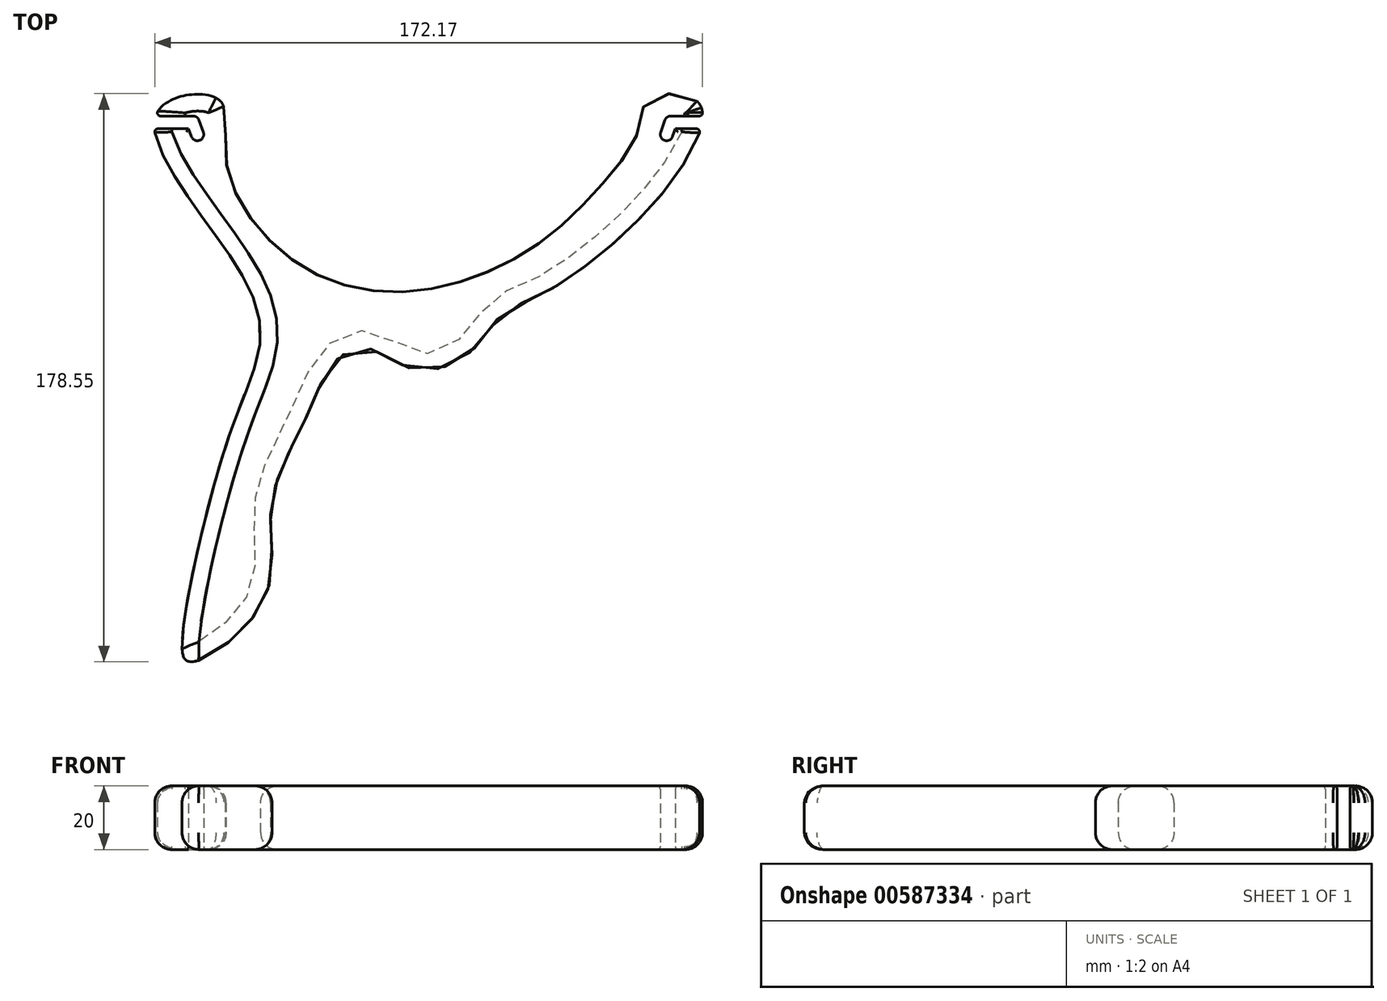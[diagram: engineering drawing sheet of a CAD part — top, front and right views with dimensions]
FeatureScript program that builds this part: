
annotation { "Feature Type Name" : "Feature", "Feature Type Description" : "" }
export const myFeature = defineFeature(function(context is Context, id is Id, definition is map)
    precondition{}
    {
        {
            var Q0;
            Q0=qCreatedBy(makeId("Top.planeOp"),FACE);
            var sketch = newSketch(context, id + "F0", { "sketchPlane" : qUnion([Q0])});
            skFitSpline(sketch, "E0", {"points": [v(-47.93, -12.17) * mm, v(-57.47, -39.46) * mm, v(-72.05, -102.78) * mm, v(-69.37, -109.92) * mm, v(-46.47, -90.68) * mm, v(-44.04, -60.37) * mm, v(-33.84, -34.8) * mm, v(-25.4, -17.36) * mm, v(-14.64, -11.28) * mm, v(2.1, -18.27) * mm, v(21.1, -10.15) * mm, v(28.84, 0) * mm, v(37.64, 3.9) * mm, v(75.58, 33.49) * mm, v(90.24, 65.72) * mm, v(74.78, 66.75) * mm, v(71.07, 56.48) * mm, v(59.13, 39.35) * mm, v(42.22, 23.11) * mm, v(9.4, 7.88) * mm, v(-32.22, 13.06) * mm, v(-58.26, 46.98) * mm, v(-60.8, 66.85) * mm, v(-80.26, 62.1) * mm, v(-53.82, 12.56) * mm, v(-47.93, -12.17) * mm]});
            skLineSegment(sketch, "E1.bottom", {"start": v(-50.8, -23.67) * mm, "end": v(-15.8, -23.67) * mm, "construction": true});
            skLineSegment(sketch, "E1.top", {"start": v(-50.8, -113.67) * mm, "end": v(-15.8, -113.67) * mm, "construction": true});
            skLineSegment(sketch, "E1.left", {"start": v(-50.8, -23.67) * mm, "end": v(-50.8, -113.67) * mm, "construction": true});
            skLineSegment(sketch, "E1.right", {"start": v(-15.8, -23.67) * mm, "end": v(-15.8, -113.67) * mm, "construction": true});
            skLineSegment(sketch, "E2", {"start": v(4, -25.72) * mm, "end": v(34, -25.72) * mm, "construction": true});
            skLineSegment(sketch, "E3", {"start": v(-54.68, 63.24) * mm, "end": v(65.32, 63.24) * mm, "construction": true});
            skLineSegment(sketch, "E4", {"start": v(96.78, 66.75) * mm, "end": v(96.78, 6.75) * mm, "construction": true});
            skSolve(sketch);
        }
        {
            var Q0;
            Q0=makeQuery(id+"F0.imprint","IMPRINT",FACE,{"disambiguationData":[TD([[makeQuery(id+"F0.imprint","IMPRINT",EDGE,{"derivedFrom":sQuery(id+"F0.wireOp",EDGE,"E0")}),1.0]])]});
            var sketch = newSketch(context, id + "F1", { "sketchPlane" : qUnion([Q0])});
            skLineSegment(sketch, "E5", {"start": v(-68.65, 59.57) * mm, "end": v(-67.3, 55.8) * mm});
            skArc(sketch, "E6.0.startCap", {"start": v(-70.53, 58.9) * mm, "mid": v(-69.32, 61.45) * mm, "end": v(-66.77, 60.24) * mm});
            skArc(sketch, "E6.0.endCap", {"start": v(-65.42, 56.48) * mm, "mid": v(-66.63, 53.92) * mm, "end": v(-69.18, 55.13) * mm});
            skLineSegment(sketch, "E6.0.left", {"start": v(-66.77, 60.24) * mm, "end": v(-65.42, 56.48) * mm});
            skLineSegment(sketch, "E6.0.right", {"start": v(-70.53, 58.9) * mm, "end": v(-69.18, 55.13) * mm});
            skLineSegment(sketch, "E7.MirrorCS", {"start": v(81.52, 59.57) * mm, "end": v(80.18, 55.8) * mm});
            skArc(sketch, "E8.0.startCap", {"start": v(79.64, 60.24) * mm, "mid": v(82.2, 61.45) * mm, "end": v(83.4, 58.9) * mm});
            skArc(sketch, "E8.0.endCap", {"start": v(82.06, 55.13) * mm, "mid": v(79.5, 53.92) * mm, "end": v(78.3, 56.48) * mm});
            skLineSegment(sketch, "E8.0.left", {"start": v(83.4, 58.9) * mm, "end": v(82.06, 55.13) * mm});
            skLineSegment(sketch, "E8.0.right", {"start": v(79.64, 60.24) * mm, "end": v(78.3, 56.48) * mm});
            skLineSegment(sketch, "E9", {"start": v(-67.3, 55.8) * mm, "end": v(80.18, 55.8) * mm, "construction": true});
            skLineSegment(sketch, "E10", {"start": v(81.52, 59.57) * mm, "end": v(92.32, 59.57) * mm});
            skArc(sketch, "E11.0.startCap", {"start": v(81.52, 57.57) * mm, "mid": v(79.52, 59.57) * mm, "end": v(81.52, 61.57) * mm});
            skArc(sketch, "E11.0.endCap", {"start": v(92.32, 61.57) * mm, "mid": v(94.32, 59.57) * mm, "end": v(92.32, 57.57) * mm});
            skLineSegment(sketch, "E11.0.left", {"start": v(81.52, 61.57) * mm, "end": v(92.32, 61.57) * mm});
            skLineSegment(sketch, "E11.0.right", {"start": v(81.52, 57.57) * mm, "end": v(92.32, 57.57) * mm});
            skLineSegment(sketch, "E12", {"start": v(-68.65, 59.57) * mm, "end": v(-88.7, 59.57) * mm});
            skArc(sketch, "E13.0.startCap", {"start": v(-68.65, 61.57) * mm, "mid": v(-66.65, 59.57) * mm, "end": v(-68.65, 57.57) * mm});
            skArc(sketch, "E13.0.endCap", {"start": v(-88.7, 57.57) * mm, "mid": v(-90.7, 59.57) * mm, "end": v(-88.7, 61.57) * mm});
            skLineSegment(sketch, "E13.0.left", {"start": v(-68.65, 57.57) * mm, "end": v(-88.7, 57.57) * mm});
            skLineSegment(sketch, "E13.0.right", {"start": v(-68.65, 61.57) * mm, "end": v(-88.7, 61.57) * mm});
            skSolve(sketch);
        }
        {
            var Q0;
            Q0=makeQuery(id+"F0.imprint","IMPRINT",FACE,{"disambiguationData":[TD([[makeQuery(id+"F0.imprint","IMPRINT",EDGE,{"derivedFrom":sQuery(id+"F0.wireOp",EDGE,"E0")}),1.0]])]});
            extrude(context, id + "F2", {"entities" : qUnion([Q0]), "depth" : 20 * mm, "offsetDistance" : 25 * mm});
        }
        {
            var Q0;
            Q0=makeQuery(id+"F2.opExtrude","CAP_EDGE",EDGE,{"disambiguationData":[OSD([sQuery(id+"F0.wireOp",EDGE,"E0")])],"isStart":false});
            var Q1;
            Q1=makeQuery(id+"F2.opExtrude","CAP_EDGE",EDGE,{"disambiguationData":[OSD([sQuery(id+"F0.wireOp",EDGE,"E0")])],"isStart":true});
            fillet(context, id + "F3", {"entities" : qUnion([Q0, Q1]), "radius" : 5.3 * mm, "tangentPropagation" : true, "allowEdgeOverflow" : false});
        }
        {
            var Q0;
            Q0 = qSketchRegion(id + "F1", true);
            extrude(context, id + "F4", {"entities" : qUnion([Q0]), "operationType" : NewBodyOperationType.REMOVE, "endBound" : BoundingType.THROUGH_ALL, "depth" : 25 * mm, "offsetDistance" : 25 * mm});
        }
        {
            var Q0;
            Q0=makeQuery(id+"F4.boolean.opBoolean","INTERSECT",EDGE,{"derivedFrom":[makeQuery(id+"F2.opExtrude","CAP_FACE",FACE,{"disambiguationData":[OSD([sQuery(id+"F0.wireOp",EDGE,"E0")])],"isStart":false}),makeQuery(id+"F4.opExtrude","SWEPT_FACE",FACE,{"disambiguationData":[OSD([sQuery(id+"F1.wireOp",EDGE,"E6.0.right")])]})]});
            var Q1;
            {var subQ0=sQuery(id+"F0.wireOp",EDGE,"E0");Q1=makeQuery(id+"F4.boolean.opBoolean","INTERSECT",EDGE,{"derivedFrom":[makeQuery(id+"F3.opFillet","BLEND_FACE",FACE,{"disambiguationData":[OSD([subQ0]),TDD([makeQuery(id+"F2.opExtrude","CAP_EDGE",EDGE,{"disambiguationData":[OSD([subQ0])],"isStart":true})]),OD(6.0)]}),makeQuery(id+"F4.opExtrude","SWEPT_FACE",FACE,{"disambiguationData":[OSD([sQuery(id+"F1.wireOp",EDGE,"E6.0.left")])]})]});}
            var Q2;
            Q2=makeQuery(id+"F4.boolean.opBoolean","COPY",EDGE,{"derivedFrom":makeQuery(id+"F4.opExtrude","CAP_EDGE",EDGE,{"disambiguationData":[OSD([sQuery(id+"F1.wireOp",EDGE,"E8.0.right")])],"isStart":true})});
            var Q3;
            Q3=makeQuery(id+"F4.boolean.opBoolean","INTERSECT",EDGE,{"derivedFrom":[makeQuery(id+"F2.opExtrude","CAP_FACE",FACE,{"disambiguationData":[OSD([sQuery(id+"F0.wireOp",EDGE,"E0")])],"isStart":false}),makeQuery(id+"F4.opExtrude","SWEPT_FACE",FACE,{"disambiguationData":[OSD([sQuery(id+"F1.wireOp",EDGE,"E8.0.left")])]})]});
            var Q4;
            Q4=makeQuery(id+"F4.boolean.opBoolean","INTERSECT",EDGE,{"derivedFrom":[makeQuery(id+"F2.opExtrude","CAP_FACE",FACE,{"disambiguationData":[OSD([sQuery(id+"F0.wireOp",EDGE,"E0")])],"isStart":false}),makeQuery(id+"F4.opExtrude","SWEPT_FACE",FACE,{"disambiguationData":[OSD([sQuery(id+"F1.wireOp",EDGE,"E13.0.left")])]})]});
            var Q5;
            {var subQ0=sQuery(id+"F0.wireOp",EDGE,"E0");Q5=makeQuery(id+"F4.boolean.opBoolean","INTERSECT",EDGE,{"derivedFrom":[makeQuery(id+"F3.opFillet","BLEND_FACE",FACE,{"disambiguationData":[OSD([subQ0]),TDD([makeQuery(id+"F2.opExtrude","CAP_EDGE",EDGE,{"disambiguationData":[OSD([subQ0])],"isStart":false})]),OD(7.0)]}),makeQuery(id+"F4.opExtrude","SWEPT_FACE",FACE,{"disambiguationData":[OSD([sQuery(id+"F1.wireOp",EDGE,"E11.0.right")])]})]});}
            fillet(context, id + "F5", {"entities" : qUnion([Q0, Q1, Q2, Q3, Q4, Q5]), "radius" : 1 * mm, "tangentPropagation" : true, "allowEdgeOverflow" : false});
        }
    });
